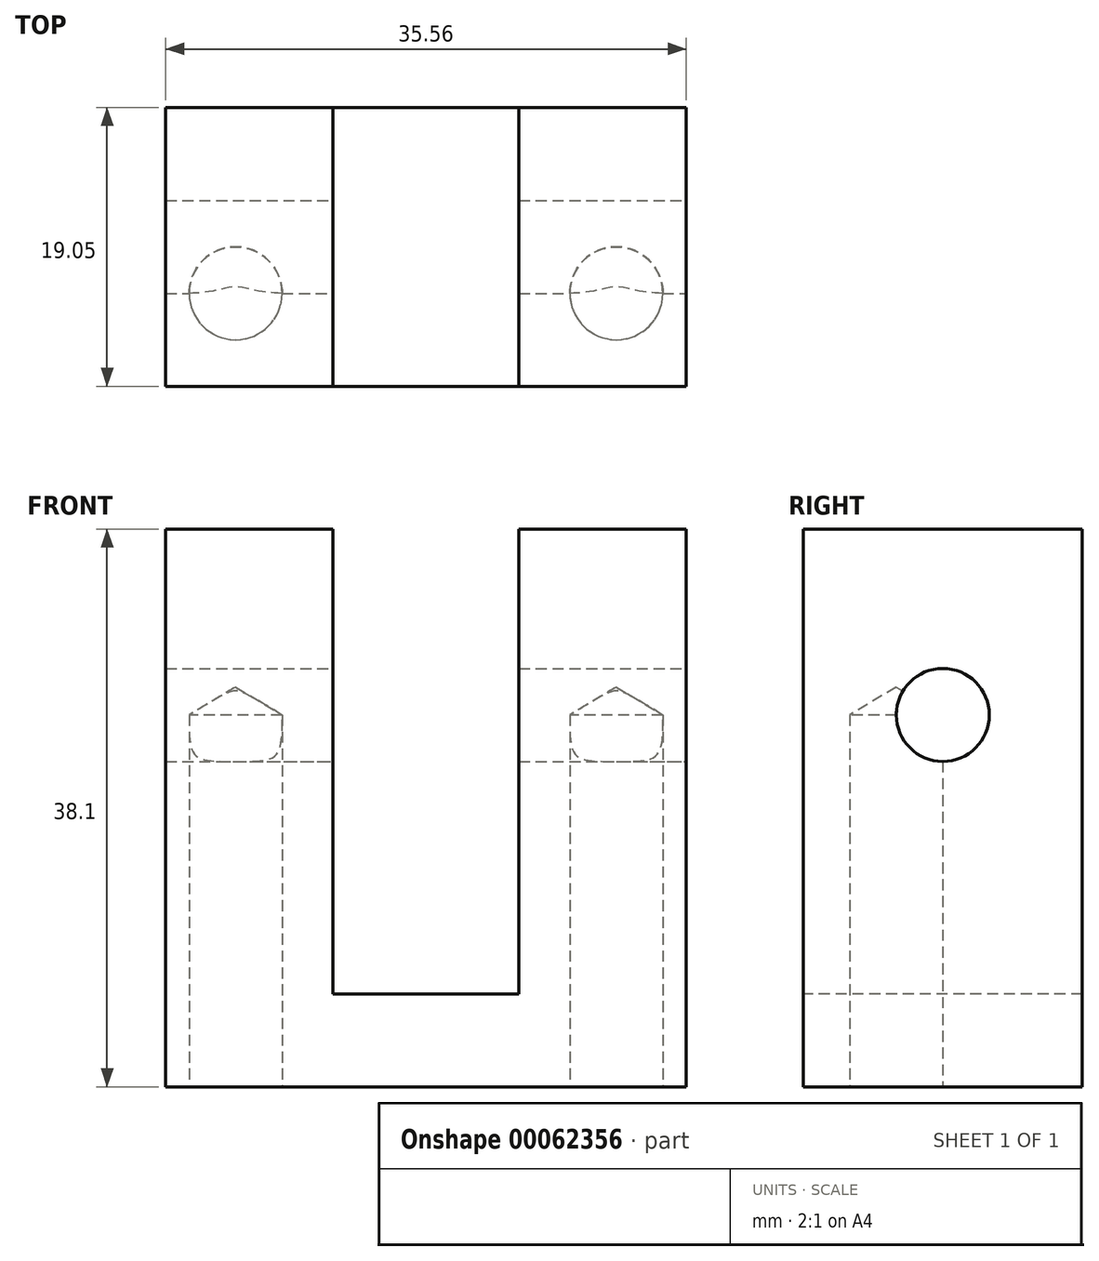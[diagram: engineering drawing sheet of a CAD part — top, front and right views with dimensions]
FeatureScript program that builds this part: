
annotation { "Feature Type Name" : "Feature", "Feature Type Description" : "" }
export const myFeature = defineFeature(function(context is Context, id is Id, definition is map)
    precondition{}
    {
        {
            var Q0;
            Q0=qCreatedBy(makeId("Front.planeOp"),FACE);
            var sketch = newSketch(context, id + "F0", { "sketchPlane" : qUnion([Q0])});
            skLineSegment(sketch, "E0", {"start": v(-17.78, 12.7) * mm, "end": v(-17.78, -25.4) * mm});
            skLineSegment(sketch, "E1", {"start": v(-17.78, -25.4) * mm, "end": v(17.78, -25.4) * mm});
            skLineSegment(sketch, "E2", {"start": v(17.78, -25.4) * mm, "end": v(17.78, 12.7) * mm});
            skLineSegment(sketch, "E3", {"start": v(17.78, 12.7) * mm, "end": v(6.35, 12.7) * mm});
            skLineSegment(sketch, "E4", {"start": v(6.35, 12.7) * mm, "end": v(6.35, -19.05) * mm});
            skLineSegment(sketch, "E5", {"start": v(6.35, -19.05) * mm, "end": v(-6.35, -19.05) * mm});
            skLineSegment(sketch, "E6", {"start": v(-6.35, -19.05) * mm, "end": v(-6.35, 12.7) * mm});
            skLineSegment(sketch, "E7", {"start": v(-6.35, 12.7) * mm, "end": v(-17.78, 12.7) * mm});
            skSolve(sketch);
        }
        {
            var Q0;
            Q0=makeQuery(id+"F0.imprint","IMPRINT",FACE,{"disambiguationData":[TD([[makeQuery(id+"F0.imprint","IMPRINT",EDGE,{"derivedFrom":sQuery(id+"F0.wireOp",EDGE,"E0")}),1.0]])]});
            extrude(context, id + "F1", {"entities" : qUnion([Q0]), "oppositeDirection" : true, "depth" : 19.05 * mm});
        }
        {
            var Q0;
            Q0=makeQuery(id+"F1.opExtrude","SWEPT_FACE",FACE,{"disambiguationData":[OSD([sQuery(id+"F0.wireOp",EDGE,"E2")])]});
            var sketch = newSketch(context, id + "F2", { "sketchPlane" : qUnion([Q0])});
            skCircle(sketch, "E8", {"center": v(9.53, 0) * mm, "radius": 3.18 * mm});
            skSolve(sketch);
        }
        {
            var Q0;
            Q0=sQuery(id+"F2.wireOp",VERTEX,"E8.center");
            var Q1;
            Q1=makeQuery(id+"F1.opExtrude","SWEPT_BODY",BODY,{"disambiguationData":[OSD([sQuery(id+"F0.wireOp",EDGE,"E0"),sQuery(id+"F0.wireOp",EDGE,"E1"),sQuery(id+"F0.wireOp",EDGE,"E2"),sQuery(id+"F0.wireOp",EDGE,"E3"),sQuery(id+"F0.wireOp",EDGE,"E4"),sQuery(id+"F0.wireOp",EDGE,"E5"),sQuery(id+"F0.wireOp",EDGE,"E6"),sQuery(id+"F0.wireOp",EDGE,"E7")])]});
            hole(context, id + "F3", {"style" : HoleStyle.SIMPLE, "holeDiameter" : 6.35 * mm, "endStyle" : HoleEndStyle.THROUGH, "locations" : qUnion([Q0]), "scope" : qUnion([Q1])});
        }
        {
            var Q0;
            Q0=makeQuery(id+"F1.opExtrude","SWEPT_FACE",FACE,{"disambiguationData":[OSD([sQuery(id+"F0.wireOp",EDGE,"E1")])]});
            var sketch = newSketch(context, id + "F4", { "sketchPlane" : qUnion([Q0])});
            skCircle(sketch, "E9", {"center": v(-13, -6.35) * mm, "radius": 3.18 * mm});
            skCircle(sketch, "E10", {"center": v(13, -6.35) * mm, "radius": 3.18 * mm});
            skSolve(sketch);
        }
        {
            var Q0;
            Q0=sQuery(id+"F4.wireOp",VERTEX,"E9.center");
            var Q1;
            Q1=sQuery(id+"F4.wireOp",VERTEX,"E10.center");
            var Q2;
            Q2=makeQuery(id+"F1.opExtrude","SWEPT_BODY",BODY,{"disambiguationData":[OSD([sQuery(id+"F0.wireOp",EDGE,"E0"),sQuery(id+"F0.wireOp",EDGE,"E1"),sQuery(id+"F0.wireOp",EDGE,"E2"),sQuery(id+"F0.wireOp",EDGE,"E3"),sQuery(id+"F0.wireOp",EDGE,"E4"),sQuery(id+"F0.wireOp",EDGE,"E5"),sQuery(id+"F0.wireOp",EDGE,"E6"),sQuery(id+"F0.wireOp",EDGE,"E7")])]});
            hole(context, id + "F5", {"style" : HoleStyle.SIMPLE, "holeDiameter" : 6.35 * mm, "endStyle" : HoleEndStyle.BLIND, "holeDepth" : 25.4 * mm, "locations" : qUnion([Q0, Q1]), "scope" : qUnion([Q2])});
        }
    });
